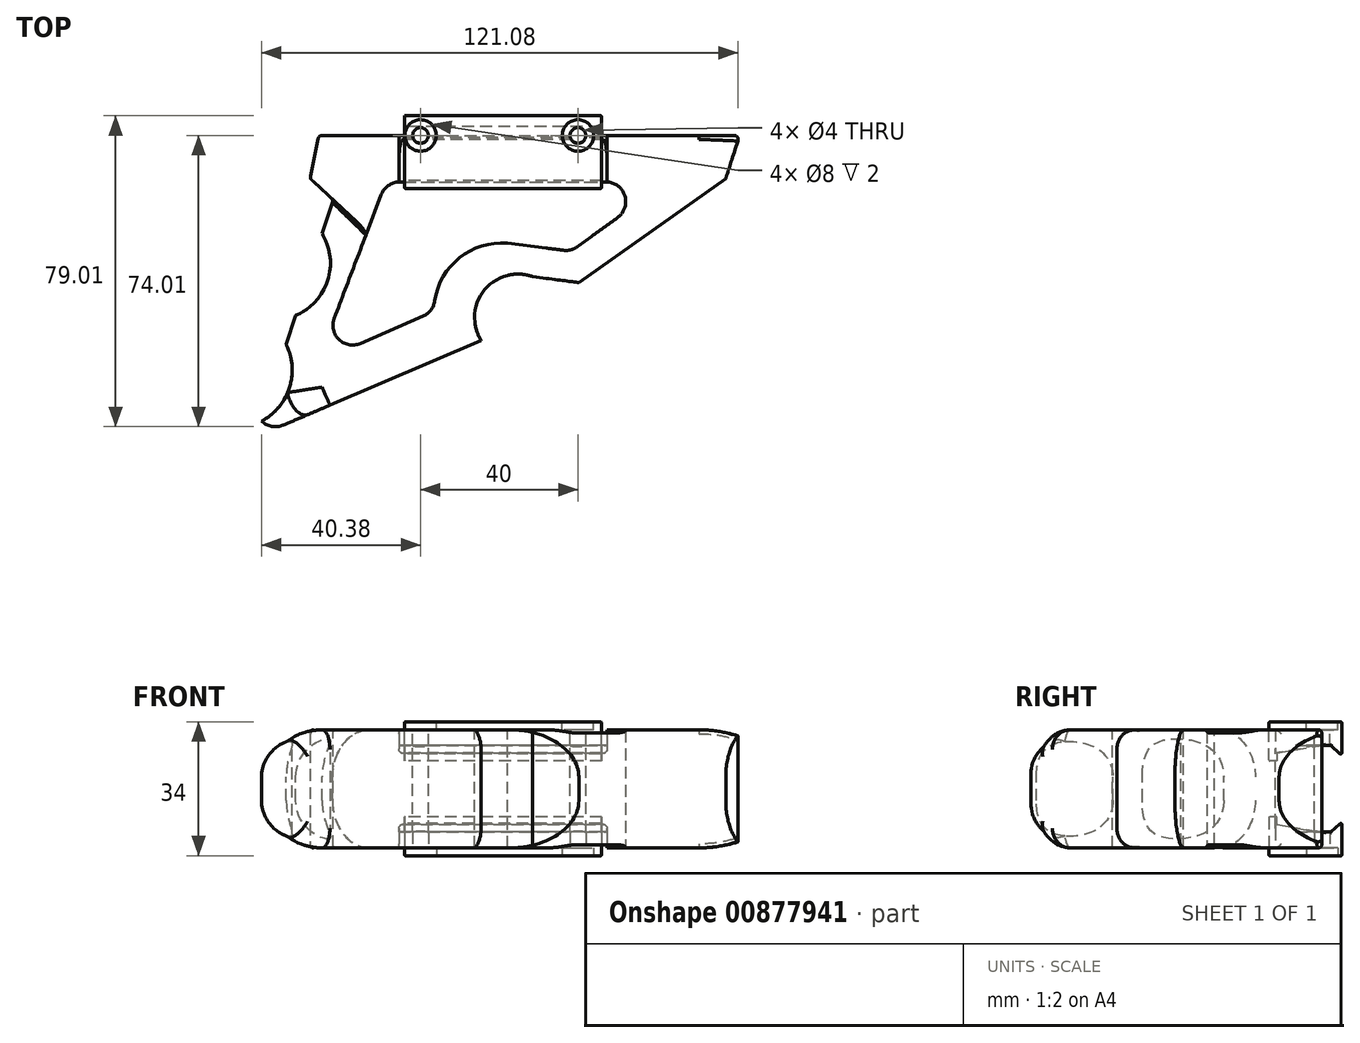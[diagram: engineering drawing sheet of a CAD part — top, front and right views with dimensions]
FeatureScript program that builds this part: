
annotation { "Feature Type Name" : "Feature", "Feature Type Description" : "" }
export const myFeature = defineFeature(function(context is Context, id is Id, definition is map)
    precondition{}
    {
        {
            var Q0;
            Q0=qCreatedBy(makeId("Top.planeOp"),FACE);
            var sketch = newSketch(context, id + "F0", { "sketchPlane" : qUnion([Q0])});
            skLineSegment(sketch, "E0", {"start": v(-36.24, 0) * mm, "end": v(-38.5, -10.92) * mm});
            skLineSegment(sketch, "E1", {"start": v(-38.5, -10.92) * mm, "end": v(-32.62, -16.35) * mm});
            skLineSegment(sketch, "E2", {"start": v(-32.62, -16.35) * mm, "end": v(-63.6, -112.26) * mm});
            skLineSegment(sketch, "E3", {"start": v(-63.6, -112.26) * mm, "end": v(-7.96, -123.8) * mm});
            skLineSegment(sketch, "E4", {"start": v(-7.96, -123.8) * mm, "end": v(16.02, -35.58) * mm});
            skLineSegment(sketch, "E5", {"start": v(16.02, -35.58) * mm, "end": v(29.82, -37.39) * mm});
            skLineSegment(sketch, "E6", {"start": v(29.82, -37.39) * mm, "end": v(67.14, -10.92) * mm});
            skLineSegment(sketch, "E7", {"start": v(67.14, -10.92) * mm, "end": v(70.67, 0) * mm});
            skLineSegment(sketch, "E8", {"start": v(-36.24, 0) * mm, "end": v(70.67, 0) * mm});
            skPoint(sketch, "E9.first.point", {"position": v(-35.48, -25.23) * mm});
            skPoint(sketch, "E9.second.point", {"position": v(-42.4, -46.63) * mm});
            skPoint(sketch, "E9.third.point", {"position": v(-65.03, -33.08) * mm});
            skPoint(sketch, "E10.first.point", {"position": v(-44.67, -53.65) * mm});
            skPoint(sketch, "E10.second.point", {"position": v(-50.9, -72.91) * mm});
            skPoint(sketch, "E10.third.point", {"position": v(-72.52, -56.97) * mm});
            skPoint(sketch, "E11.first.point", {"position": v(-54.13, -82.94) * mm});
            skPoint(sketch, "E11.second.point", {"position": v(-59.89, -100.75) * mm});
            skPoint(sketch, "E11.third.point", {"position": v(-85, -82.64) * mm});
            skLineSegment(sketch, "E12", {"start": v(-97.37, -25.23) * mm, "end": v(-7.02, -25.23) * mm, "construction": true});
            skLineSegment(sketch, "E13", {"start": v(-95.85, -46.63) * mm, "end": v(-7.4, -46.63) * mm, "construction": true});
            skLineSegment(sketch, "E14", {"start": v(-81.01, -53.65) * mm, "end": v(-12.15, -53.65) * mm, "construction": true});
            skLineSegment(sketch, "E15", {"start": v(-92.8, -72.91) * mm, "end": v(-15.2, -72.91) * mm, "construction": true});
            skLineSegment(sketch, "E16", {"start": v(-54.13, -82.94) * mm, "end": v(-73.21, -82.94) * mm});
            skLineSegment(sketch, "E17", {"start": v(-73.21, -82.94) * mm, "end": v(-28.9, -82.94) * mm, "construction": true});
            skLineSegment(sketch, "E18", {"start": v(-59.89, -100.75) * mm, "end": v(-91.1, -100.75) * mm});
            skLineSegment(sketch, "E19", {"start": v(-91.1, -100.75) * mm, "end": v(-23.57, -100.75) * mm, "construction": true});
            skLineSegment(sketch, "E20", {"start": v(-30.41, -25.23) * mm, "end": v(-60.21, -112.97) * mm, "construction": true});
            skSolve(sketch);
        }
        {
            var Q0;
            Q0=qSketchRegion(id+"F0",true);
            extrude(context, id + "F1", {"entities" : qUnion([Q0]), "endBound" : BoundingType.SYMMETRIC, "depth" : 30 * mm, "offsetDistance" : 25 * mm});
        }
        {
            var Q0;
            Q0=qCreatedBy(makeId("Top.planeOp"),FACE);
            var sketch = newSketch(context, id + "F2", { "sketchPlane" : qUnion([Q0])});
            skCircle(sketch, "E21", {"center": v(-47.66, -32.46) * mm, "radius": 14.36 * mm});
            skPoint(sketch, "E21.first.point", {"position": v(-35.59, -24.68) * mm});
            skPoint(sketch, "E21.second.point", {"position": v(-43.3, -46.15) * mm});
            skPoint(sketch, "E21.third.point", {"position": v(-61.39, -28.25) * mm});
            skCircle(sketch, "E22", {"center": v(-57.68, -59.62) * mm, "radius": 14.67 * mm});
            skPoint(sketch, "E22.first.point", {"position": v(-44.44, -53.3) * mm});
            skPoint(sketch, "E22.second.point", {"position": v(-51.03, -72.7) * mm});
            skPoint(sketch, "E22.third.point", {"position": v(-72.31, -58.58) * mm});
            skCircle(sketch, "E23", {"center": v(-69.65, -87.55) * mm, "radius": 16.16 * mm});
            skPoint(sketch, "E23.first.point", {"position": v(-54.23, -82.68) * mm});
            skPoint(sketch, "E23.second.point", {"position": v(-60.07, -100.57) * mm});
            skPoint(sketch, "E23.third.point", {"position": v(-85.5, -84.38) * mm});
            skCircle(sketch, "E24", {"center": v(-22.89, -107.96) * mm, "radius": 8.48 * mm});
            skPoint(sketch, "E24.first.point", {"position": v(-24.85, -116.2) * mm});
            skPoint(sketch, "E24.second.point", {"position": v(-20.52, -99.82) * mm});
            skPoint(sketch, "E24.third.point", {"position": v(-15.62, -103.59) * mm});
            skCircle(sketch, "E25", {"center": v(14.39, -46.27) * mm, "radius": 11.05 * mm});
            skPoint(sketch, "E25.first.point", {"position": v(16.03, -35.34) * mm});
            skPoint(sketch, "E25.second.point", {"position": v(10.2, -56.5) * mm});
            skPoint(sketch, "E25.third.point", {"position": v(23.76, -52.13) * mm});
            skCircle(sketch, "E26", {"center": v(14.16, -70.47) * mm, "radius": 11.31 * mm});
            skPoint(sketch, "E26.first.point", {"position": v(9.42, -60.2) * mm});
            skPoint(sketch, "E26.second.point", {"position": v(5.17, -77.33) * mm});
            skPoint(sketch, "E26.third.point", {"position": v(24.99, -73.75) * mm});
            skCircle(sketch, "E27", {"center": v(5.4, -101.86) * mm, "radius": 14.2 * mm});
            skPoint(sketch, "E27.first.point", {"position": v(2, -88.08) * mm});
            skPoint(sketch, "E27.second.point", {"position": v(-4.5, -112.05) * mm});
            skPoint(sketch, "E27.third.point", {"position": v(18.9, -106.22) * mm});
            skSolve(sketch);
        }
        {
            var Q0;
            Q0=qSketchRegion(id+"F2",true);
            extrude(context, id + "F3", {"entities" : qUnion([Q0]), "operationType" : NewBodyOperationType.REMOVE, "endBound" : BoundingType.SYMMETRIC, "oppositeDirection" : true, "depth" : 30 * mm, "offsetDistance" : 25 * mm});
        }
        {
            var Q0;
            {var subQ0=sQuery(id+"F2.wireOp",EDGE,"E22");Q0=makeQuery(id+"F3.boolean.opBoolean","COPY",EDGE,{"derivedFrom":makeQuery(id+"F3.opExtrude","CAP_EDGE",EDGE,{"disambiguationData":[OSD([subQ0]),TDD([makeQuery(id+"F2.imprint","IMPRINT",EDGE,{"disambiguationData":[TD([[makeQuery(id+"F2.imprint","INTERSECT",VERTEX,{"disambiguationData":[OD(1.0)],"derivedFrom":[sQuery(id+"F2.wireOp",EDGE,"E21"),subQ0]}),1.0]])],"derivedFrom":subQ0})])],"isStart":true})});}
            var Q1;
            Q1=makeQuery(id+"F3.boolean.opBoolean","COPY",EDGE,{"derivedFrom":makeQuery(id+"F3.opExtrude","CAP_EDGE",EDGE,{"disambiguationData":[OSD([sQuery(id+"F2.wireOp",EDGE,"E21")])],"isStart":true})});
            var Q2;
            Q2=makeQuery(id+"F3.boolean.opBoolean","COPY",EDGE,{"derivedFrom":makeQuery(id+"F3.opExtrude","CAP_EDGE",EDGE,{"disambiguationData":[OSD([sQuery(id+"F2.wireOp",EDGE,"E23")])],"isStart":true})});
            var Q3;
            Q3=makeQuery(id+"F3.boolean.opBoolean","COPY",EDGE,{"derivedFrom":makeQuery(id+"F3.opExtrude","CAP_EDGE",EDGE,{"disambiguationData":[OSD([sQuery(id+"F2.wireOp",EDGE,"E21")])],"isStart":false})});
            var Q4;
            {var subQ0=sQuery(id+"F2.wireOp",EDGE,"E22");Q4=makeQuery(id+"F3.boolean.opBoolean","COPY",EDGE,{"derivedFrom":makeQuery(id+"F3.opExtrude","CAP_EDGE",EDGE,{"disambiguationData":[OSD([subQ0]),TDD([makeQuery(id+"F2.imprint","IMPRINT",EDGE,{"disambiguationData":[TD([[makeQuery(id+"F2.imprint","INTERSECT",VERTEX,{"disambiguationData":[OD(1.0)],"derivedFrom":[sQuery(id+"F2.wireOp",EDGE,"E21"),subQ0]}),1.0]])],"derivedFrom":subQ0})])],"isStart":false})});}
            var Q5;
            Q5=makeQuery(id+"F3.boolean.opBoolean","COPY",EDGE,{"derivedFrom":makeQuery(id+"F3.opExtrude","CAP_EDGE",EDGE,{"disambiguationData":[OSD([sQuery(id+"F2.wireOp",EDGE,"E23")])],"isStart":false})});
            var Q6;
            {var subQ0=sQuery(id+"F0.wireOp",EDGE,"E2");var subQ1=sQuery(id+"F2.wireOp",EDGE,"E22");var subQ2=sQuery(id+"F2.wireOp",EDGE,"E23");Q6=makeQuery(id+"F3.boolean.opBoolean","SPLIT",EDGE,{"disambiguationData":[TD([makeQuery(id+"F1.opExtrude","CAP_FACE",FACE,{"disambiguationData":[OSD([sQuery(id+"F0.wireOp",EDGE,"E0"),sQuery(id+"F0.wireOp",EDGE,"E1"),subQ0,sQuery(id+"F0.wireOp",EDGE,"E3"),sQuery(id+"F0.wireOp",EDGE,"E4"),sQuery(id+"F0.wireOp",EDGE,"E5"),sQuery(id+"F0.wireOp",EDGE,"E6"),sQuery(id+"F0.wireOp",EDGE,"E7"),sQuery(id+"F0.wireOp",EDGE,"E8")])],"isStart":false}),makeQuery(id+"F1.opExtrude","SWEPT_FACE",FACE,{"disambiguationData":[OSD([subQ0])]}),makeQuery(id+"F3.opExtrude","SWEPT_FACE",FACE,{"disambiguationData":[OSD([subQ1]),TDD([makeQuery(id+"F2.imprint","IMPRINT",EDGE,{"disambiguationData":[TD([[makeQuery(id+"F2.imprint","INTERSECT",VERTEX,{"disambiguationData":[OD(1.0)],"derivedFrom":[sQuery(id+"F2.wireOp",EDGE,"E21"),subQ1]}),1.0]])],"derivedFrom":subQ1})])]}),makeQuery(id+"F3.opExtrude","SWEPT_FACE",FACE,{"disambiguationData":[OSD([subQ2])]})])],"derivedFrom":makeQuery(id+"F1.opExtrude","CAP_EDGE",EDGE,{"disambiguationData":[OSD([subQ0])],"isStart":false})});}
            var Q7;
            {var subQ0=sQuery(id+"F0.wireOp",EDGE,"E2");var subQ1=sQuery(id+"F2.wireOp",EDGE,"E22");var subQ2=sQuery(id+"F2.wireOp",EDGE,"E21");Q7=makeQuery(id+"F3.boolean.opBoolean","SPLIT",EDGE,{"disambiguationData":[TD([makeQuery(id+"F1.opExtrude","CAP_FACE",FACE,{"disambiguationData":[OSD([sQuery(id+"F0.wireOp",EDGE,"E0"),sQuery(id+"F0.wireOp",EDGE,"E1"),subQ0,sQuery(id+"F0.wireOp",EDGE,"E3"),sQuery(id+"F0.wireOp",EDGE,"E4"),sQuery(id+"F0.wireOp",EDGE,"E5"),sQuery(id+"F0.wireOp",EDGE,"E6"),sQuery(id+"F0.wireOp",EDGE,"E7"),sQuery(id+"F0.wireOp",EDGE,"E8")])],"isStart":false}),makeQuery(id+"F1.opExtrude","SWEPT_FACE",FACE,{"disambiguationData":[OSD([subQ0])]}),makeQuery(id+"F3.opExtrude","SWEPT_FACE",FACE,{"disambiguationData":[OSD([subQ2])]}),makeQuery(id+"F3.opExtrude","SWEPT_FACE",FACE,{"disambiguationData":[OSD([subQ1]),TDD([makeQuery(id+"F2.imprint","IMPRINT",EDGE,{"disambiguationData":[TD([[makeQuery(id+"F2.imprint","INTERSECT",VERTEX,{"disambiguationData":[OD(1.0)],"derivedFrom":[subQ2,subQ1]}),1.0]])],"derivedFrom":subQ1})])]})])],"derivedFrom":makeQuery(id+"F1.opExtrude","CAP_EDGE",EDGE,{"disambiguationData":[OSD([subQ0])],"isStart":false})});}
            var Q8;
            {var subQ0=sQuery(id+"F0.wireOp",EDGE,"E2");var subQ1=sQuery(id+"F2.wireOp",EDGE,"E22");var subQ2=sQuery(id+"F2.wireOp",EDGE,"E23");Q8=makeQuery(id+"F3.boolean.opBoolean","SPLIT",EDGE,{"disambiguationData":[TD([makeQuery(id+"F1.opExtrude","CAP_FACE",FACE,{"disambiguationData":[OSD([sQuery(id+"F0.wireOp",EDGE,"E0"),sQuery(id+"F0.wireOp",EDGE,"E1"),subQ0,sQuery(id+"F0.wireOp",EDGE,"E3"),sQuery(id+"F0.wireOp",EDGE,"E4"),sQuery(id+"F0.wireOp",EDGE,"E5"),sQuery(id+"F0.wireOp",EDGE,"E6"),sQuery(id+"F0.wireOp",EDGE,"E7"),sQuery(id+"F0.wireOp",EDGE,"E8")])],"isStart":true}),makeQuery(id+"F1.opExtrude","SWEPT_FACE",FACE,{"disambiguationData":[OSD([subQ0])]}),makeQuery(id+"F3.opExtrude","SWEPT_FACE",FACE,{"disambiguationData":[OSD([subQ1]),TDD([makeQuery(id+"F2.imprint","IMPRINT",EDGE,{"disambiguationData":[TD([[makeQuery(id+"F2.imprint","INTERSECT",VERTEX,{"disambiguationData":[OD(1.0)],"derivedFrom":[sQuery(id+"F2.wireOp",EDGE,"E21"),subQ1]}),1.0]])],"derivedFrom":subQ1})])]}),makeQuery(id+"F3.opExtrude","SWEPT_FACE",FACE,{"disambiguationData":[OSD([subQ2])]})])],"derivedFrom":makeQuery(id+"F1.opExtrude","CAP_EDGE",EDGE,{"disambiguationData":[OSD([subQ0])],"isStart":true})});}
            var Q9;
            {var subQ0=sQuery(id+"F0.wireOp",EDGE,"E2");var subQ1=sQuery(id+"F2.wireOp",EDGE,"E21");var subQ2=sQuery(id+"F2.wireOp",EDGE,"E22");Q9=makeQuery(id+"F3.boolean.opBoolean","SPLIT",EDGE,{"disambiguationData":[TD([makeQuery(id+"F1.opExtrude","CAP_FACE",FACE,{"disambiguationData":[OSD([sQuery(id+"F0.wireOp",EDGE,"E0"),sQuery(id+"F0.wireOp",EDGE,"E1"),subQ0,sQuery(id+"F0.wireOp",EDGE,"E3"),sQuery(id+"F0.wireOp",EDGE,"E4"),sQuery(id+"F0.wireOp",EDGE,"E5"),sQuery(id+"F0.wireOp",EDGE,"E6"),sQuery(id+"F0.wireOp",EDGE,"E7"),sQuery(id+"F0.wireOp",EDGE,"E8")])],"isStart":true}),makeQuery(id+"F1.opExtrude","SWEPT_FACE",FACE,{"disambiguationData":[OSD([subQ0])]}),makeQuery(id+"F3.opExtrude","SWEPT_FACE",FACE,{"disambiguationData":[OSD([subQ1])]}),makeQuery(id+"F3.opExtrude","SWEPT_FACE",FACE,{"disambiguationData":[OSD([subQ2]),TDD([makeQuery(id+"F2.imprint","IMPRINT",EDGE,{"disambiguationData":[TD([[makeQuery(id+"F2.imprint","INTERSECT",VERTEX,{"disambiguationData":[OD(1.0)],"derivedFrom":[subQ1,subQ2]}),1.0]])],"derivedFrom":subQ2})])]})])],"derivedFrom":makeQuery(id+"F1.opExtrude","CAP_EDGE",EDGE,{"disambiguationData":[OSD([subQ0])],"isStart":true})});}
            var Q10;
            Q10=makeQuery(id+"F3.boolean.opBoolean","COPY",EDGE,{"derivedFrom":makeQuery(id+"F3.opExtrude","CAP_EDGE",EDGE,{"disambiguationData":[OSD([sQuery(id+"F2.wireOp",EDGE,"E25")])],"isStart":true})});
            var Q11;
            Q11=makeQuery(id+"F3.boolean.opBoolean","COPY",EDGE,{"derivedFrom":makeQuery(id+"F3.opExtrude","CAP_EDGE",EDGE,{"disambiguationData":[OSD([sQuery(id+"F2.wireOp",EDGE,"E26")])],"isStart":true})});
            var Q12;
            Q12=makeQuery(id+"F3.boolean.opBoolean","COPY",EDGE,{"derivedFrom":makeQuery(id+"F3.opExtrude","CAP_EDGE",EDGE,{"disambiguationData":[OSD([sQuery(id+"F2.wireOp",EDGE,"E27")])],"isStart":true})});
            var Q13;
            Q13=makeQuery(id+"F3.boolean.opBoolean","COPY",EDGE,{"derivedFrom":makeQuery(id+"F3.opExtrude","CAP_EDGE",EDGE,{"disambiguationData":[OSD([sQuery(id+"F2.wireOp",EDGE,"E27")])],"isStart":false})});
            var Q14;
            Q14=makeQuery(id+"F3.boolean.opBoolean","COPY",EDGE,{"derivedFrom":makeQuery(id+"F3.opExtrude","CAP_EDGE",EDGE,{"disambiguationData":[OSD([sQuery(id+"F2.wireOp",EDGE,"E26")])],"isStart":false})});
            var Q15;
            Q15=makeQuery(id+"F3.boolean.opBoolean","COPY",EDGE,{"derivedFrom":makeQuery(id+"F3.opExtrude","CAP_EDGE",EDGE,{"disambiguationData":[OSD([sQuery(id+"F2.wireOp",EDGE,"E25")])],"isStart":false})});
            var Q16;
            Q16=makeQuery(id+"F1.opExtrude","CAP_EDGE",EDGE,{"disambiguationData":[OSD([sQuery(id+"F0.wireOp",EDGE,"E6")])],"isStart":true});
            var Q17;
            Q17=makeQuery(id+"F1.opExtrude","CAP_EDGE",EDGE,{"disambiguationData":[OSD([sQuery(id+"F0.wireOp",EDGE,"E6")])],"isStart":false});
            var Q18;
            Q18=makeQuery(id+"F1.opExtrude","CAP_EDGE",EDGE,{"disambiguationData":[OSD([sQuery(id+"F0.wireOp",EDGE,"E3")])],"isStart":true});
            var Q19;
            Q19=makeQuery(id+"F1.opExtrude","CAP_EDGE",EDGE,{"disambiguationData":[OSD([sQuery(id+"F0.wireOp",EDGE,"E3")])],"isStart":false});
            fillet(context, id + "F4", {"entities" : qUnion([Q0, Q1, Q2, Q3, Q4, Q5, Q6, Q7, Q8, Q9, Q10, Q11, Q12, Q13, Q14, Q15, Q16, Q17, Q18, Q19]), "radius" : 12 * mm, "tangentPropagation" : true, "allowEdgeOverflow" : false});
        }
        {
            var Q0;
            Q0=makeQuery(id+"F1.opExtrude","SWEPT_EDGE",EDGE,{"disambiguationData":[OSD([sQuery(id+"F0.wireOp",EDGE,"E1"),sQuery(id+"F0.wireOp",EDGE,"E2")])]});
            var Q1;
            Q1=makeQuery(id+"F1.opExtrude","SWEPT_EDGE",EDGE,{"disambiguationData":[OSD([sQuery(id+"F0.wireOp",EDGE,"E0"),sQuery(id+"F0.wireOp",EDGE,"E1")])]});
            var Q2;
            Q2=makeQuery(id+"F1.opExtrude","SWEPT_EDGE",EDGE,{"disambiguationData":[OSD([sQuery(id+"F0.wireOp",EDGE,"E0"),sQuery(id+"F0.wireOp",EDGE,"E8")])]});
            var Q3;
            Q3=makeQuery(id+"F1.opExtrude","SWEPT_EDGE",EDGE,{"disambiguationData":[OSD([sQuery(id+"F0.wireOp",EDGE,"E7"),sQuery(id+"F0.wireOp",EDGE,"E8")])]});
            var Q4;
            Q4=makeQuery(id+"F1.opExtrude","CAP_EDGE",EDGE,{"disambiguationData":[OSD([sQuery(id+"F0.wireOp",EDGE,"E8")])],"isStart":false});
            var Q5;
            Q5=makeQuery(id+"F1.opExtrude","CAP_EDGE",EDGE,{"disambiguationData":[OSD([sQuery(id+"F0.wireOp",EDGE,"E8")])],"isStart":true});
            var Q6;
            Q6=makeQuery(id+"F1.opExtrude","CAP_EDGE",EDGE,{"disambiguationData":[OSD([sQuery(id+"F0.wireOp",EDGE,"E0")])],"isStart":false});
            var Q7;
            Q7=makeQuery(id+"F1.opExtrude","CAP_EDGE",EDGE,{"disambiguationData":[OSD([sQuery(id+"F0.wireOp",EDGE,"E0")])],"isStart":true});
            fillet(context, id + "F5", {"entities" : qUnion([Q0, Q1, Q2, Q3, Q4, Q5, Q6, Q7]), "radius" : 1 * mm, "tangentPropagation" : true, "allowEdgeOverflow" : false});
        }
        {
            var Q0;
            Q0=qCreatedBy(makeId("Top.planeOp"),FACE);
            var sketch = newSketch(context, id + "F6", { "sketchPlane" : qUnion([Q0])});
            skLineSegment(sketch, "E28", {"start": v(-50.63, -99.24) * mm, "end": v(-41.6, -72.02) * mm});
            skLineSegment(sketch, "E29", {"start": v(-41.6, -72.02) * mm, "end": v(-2.6, -55.36) * mm});
            skLineSegment(sketch, "E30", {"start": v(-2.6, -55.36) * mm, "end": v(-12.68, -83.42) * mm});
            skLineSegment(sketch, "E31", {"start": v(-12.68, -83.42) * mm, "end": v(-50.63, -99.24) * mm});
            skLineSegment(sketch, "E32", {"start": v(-36.57, -57.58) * mm, "end": v(-19.15, -11.81) * mm});
            skLineSegment(sketch, "E33", {"start": v(-19.15, -11.81) * mm, "end": v(52.14, -11.81) * mm});
            skLineSegment(sketch, "E34", {"start": v(52.14, -11.81) * mm, "end": v(27.84, -29.42) * mm});
            skLineSegment(sketch, "E35", {"start": v(27.84, -29.42) * mm, "end": v(11.65, -27.35) * mm});
            skLineSegment(sketch, "E36", {"start": v(-36.57, -57.58) * mm, "end": v(-7, -44.68) * mm});
            skArc(sketch, "E37", {"start": v(13.34, -27.57) * mm, "mid": v(-0.83, -31.36) * mm, "end": v(-7, -44.68) * mm});
            skPoint(sketch, "E37.third.point", {"position": v(24.64, -54.28) * mm});
            skSolve(sketch);
        }
        {
            var Q0;
            Q0=qSketchRegion(id+"F6",true);
            extrude(context, id + "F7", {"entities" : qUnion([Q0]), "operationType" : NewBodyOperationType.REMOVE, "endBound" : BoundingType.SYMMETRIC, "oppositeDirection" : true, "depth" : 30 * mm, "offsetDistance" : 25 * mm});
        }
        {
            var Q0;
            Q0=makeQuery(id+"F4.opFillet","BLEND_EDGE",EDGE,{"blendedFrom":[makeQuery(id+"F1.opExtrude","CAP_EDGE",EDGE,{"disambiguationData":[OSD([sQuery(id+"F0.wireOp",EDGE,"E3")])],"isStart":false}),makeQuery(id+"F3.boolean.opBoolean","COPY",FACE,{"derivedFrom":makeQuery(id+"F3.opExtrude","SWEPT_FACE",FACE,{"disambiguationData":[OSD([sQuery(id+"F2.wireOp",EDGE,"E24")])]})})],"blendedInto":[makeQuery(id+"F3.boolean.opBoolean","COPY",FACE,{"derivedFrom":makeQuery(id+"F3.opExtrude","SWEPT_FACE",FACE,{"disambiguationData":[OSD([sQuery(id+"F2.wireOp",EDGE,"E24")])]})})]});
            var Q1;
            Q1=makeQuery(id+"F4.opFillet","BLEND_EDGE",EDGE,{"blendedFrom":[makeQuery(id+"F1.opExtrude","CAP_EDGE",EDGE,{"disambiguationData":[OSD([sQuery(id+"F0.wireOp",EDGE,"E3")])],"isStart":true}),makeQuery(id+"F3.boolean.opBoolean","COPY",FACE,{"derivedFrom":makeQuery(id+"F3.opExtrude","SWEPT_FACE",FACE,{"disambiguationData":[OSD([sQuery(id+"F2.wireOp",EDGE,"E24")])]})})],"blendedInto":[makeQuery(id+"F3.boolean.opBoolean","COPY",FACE,{"derivedFrom":makeQuery(id+"F3.opExtrude","SWEPT_FACE",FACE,{"disambiguationData":[OSD([sQuery(id+"F2.wireOp",EDGE,"E24")])]})})]});
            fillet(context, id + "F8", {"entities" : qUnion([Q0, Q1]), "radius" : 1 * mm, "tangentPropagation" : true, "allowEdgeOverflow" : false});
        }
        {
            var Q0;
            Q0=makeQuery(id+"F7.boolean.opBoolean","COPY",EDGE,{"derivedFrom":makeQuery(id+"F7.opExtrude","SWEPT_EDGE",EDGE,{"disambiguationData":[OSD([sQuery(id+"F6.wireOp",EDGE,"E28"),sQuery(id+"F6.wireOp",EDGE,"E31")])]})});
            var Q1;
            Q1=makeQuery(id+"F7.boolean.opBoolean","COPY",EDGE,{"derivedFrom":makeQuery(id+"F7.opExtrude","SWEPT_EDGE",EDGE,{"disambiguationData":[OSD([sQuery(id+"F6.wireOp",EDGE,"E29"),sQuery(id+"F6.wireOp",EDGE,"E30")])]})});
            var Q2;
            Q2=makeQuery(id+"F7.boolean.opBoolean","COPY",EDGE,{"derivedFrom":makeQuery(id+"F7.opExtrude","SWEPT_EDGE",EDGE,{"disambiguationData":[OSD([sQuery(id+"F6.wireOp",EDGE,"E28"),sQuery(id+"F6.wireOp",EDGE,"E29")])]})});
            var Q3;
            Q3=makeQuery(id+"F7.boolean.opBoolean","COPY",EDGE,{"derivedFrom":makeQuery(id+"F7.opExtrude","SWEPT_EDGE",EDGE,{"disambiguationData":[OSD([sQuery(id+"F6.wireOp",EDGE,"E30"),sQuery(id+"F6.wireOp",EDGE,"E31")])]})});
            var Q4;
            Q4=makeQuery(id+"F7.boolean.opBoolean","COPY",EDGE,{"derivedFrom":makeQuery(id+"F7.opExtrude","SWEPT_EDGE",EDGE,{"disambiguationData":[OSD([sQuery(id+"F6.wireOp",EDGE,"E32"),sQuery(id+"F6.wireOp",EDGE,"E36")])]})});
            var Q5;
            Q5=makeQuery(id+"F7.boolean.opBoolean","COPY",EDGE,{"derivedFrom":makeQuery(id+"F7.opExtrude","SWEPT_EDGE",EDGE,{"disambiguationData":[OSD([sQuery(id+"F6.wireOp",EDGE,"E32"),sQuery(id+"F6.wireOp",EDGE,"E33")])]})});
            var Q6;
            Q6=makeQuery(id+"F7.boolean.opBoolean","COPY",EDGE,{"derivedFrom":makeQuery(id+"F7.opExtrude","SWEPT_EDGE",EDGE,{"disambiguationData":[OSD([sQuery(id+"F6.wireOp",EDGE,"E33"),sQuery(id+"F6.wireOp",EDGE,"E34")])]})});
            var Q7;
            Q7=makeQuery(id+"F7.boolean.opBoolean","COPY",EDGE,{"derivedFrom":makeQuery(id+"F7.opExtrude","SWEPT_EDGE",EDGE,{"disambiguationData":[OSD([sQuery(id+"F6.wireOp",EDGE,"E34"),sQuery(id+"F6.wireOp",EDGE,"E35")])]})});
            var Q8;
            Q8=makeQuery(id+"F7.boolean.opBoolean","COPY",EDGE,{"derivedFrom":makeQuery(id+"F7.opExtrude","SWEPT_EDGE",EDGE,{"disambiguationData":[OSD([sQuery(id+"F6.wireOp",EDGE,"E36"),sQuery(id+"F6.wireOp",EDGE,"E37")])]})});
            fillet(context, id + "F9", {"entities" : qUnion([Q0, Q1, Q2, Q3, Q4, Q5, Q6, Q7, Q8]), "radius" : 5 * mm, "tangentPropagation" : true, "allowEdgeOverflow" : false});
        }
        {
            var Q0;
            Q0=qCreatedBy(makeId("Right.planeOp"),FACE);
            var sketch = newSketch(context, id + "F10", { "sketchPlane" : qUnion([Q0])});
            skLineSegment(sketch, "E38", {"start": v(-1, 11) * mm, "end": v(-11.96, 9.07) * mm});
            skLineSegment(sketch, "E39", {"start": v(-11.96, 13.97) * mm, "end": v(-11.96, 9.07) * mm});
            skLineSegment(sketch, "E40", {"start": v(0, 0) * mm, "end": v(-125.67, 0) * mm, "construction": true});
            skLineSegment(sketch, "E41.MirrorCS", {"start": v(-1, -11) * mm, "end": v(-11.96, -9.07) * mm});
            skLineSegment(sketch, "E42.MirrorCS", {"start": v(-1, -17.8) * mm, "end": v(-11.96, -17.8) * mm});
            skLineSegment(sketch, "E43.MirrorCS", {"start": v(-11.96, -17.8) * mm, "end": v(-11.96, -9.07) * mm});
            skLineSegment(sketch, "E44.top", {"start": v(-1, 11) * mm, "end": v(1.5, 11) * mm});
            skLineSegment(sketch, "E44.right", {"start": v(1.5, 13.97) * mm, "end": v(1.5, 11) * mm});
            skLineSegment(sketch, "E45.bottom", {"start": v(-1, -11) * mm, "end": v(1.5, -11) * mm});
            skLineSegment(sketch, "E45.top", {"start": v(-1, -17.8) * mm, "end": v(1.5, -17.8) * mm});
            skLineSegment(sketch, "E45.right", {"start": v(1.5, -11) * mm, "end": v(1.5, -17.8) * mm});
            skLineSegment(sketch, "E46.top", {"start": v(-11.96, 17.3) * mm, "end": v(1.5, 17.3) * mm});
            skLineSegment(sketch, "E46.left", {"start": v(-11.96, 13.97) * mm, "end": v(-11.96, 17.3) * mm});
            skLineSegment(sketch, "E46.right", {"start": v(1.5, 13.97) * mm, "end": v(1.5, 17.3) * mm});
            skSolve(sketch);
        }
        {
            var Q0;
            Q0=qSketchRegion(id+"F10",true);
            extrude(context, id + "F11", {"entities" : qUnion([Q0]), "operationType" : NewBodyOperationType.REMOVE, "depth" : 37 * mm, "offsetDistance" : 25 * mm, "hasSecondDirection" : true, "secondDirectionOppositeDirection" : true, "secondDirectionDepth" : 15.9 * mm});
        }
        {
            var Q0;
            Q0=makeQuery(id+"F11.boolean.opBoolean","COPY",EDGE,{"derivedFrom":makeQuery(id+"F11.opExtrude","CAP_EDGE",EDGE,{"disambiguationData":[OSD([sQuery(id+"F10.wireOp",EDGE,"E38")])],"isStart":true})});
            var Q1;
            Q1=makeQuery(id+"F11.boolean.opBoolean","COPY",EDGE,{"derivedFrom":makeQuery(id+"F11.opExtrude","CAP_EDGE",EDGE,{"disambiguationData":[OSD([sQuery(id+"F10.wireOp",EDGE,"E38")])],"isStart":false})});
            var Q2;
            Q2=makeQuery(id+"F11.boolean.opBoolean","COPY",EDGE,{"derivedFrom":makeQuery(id+"F11.opExtrude","CAP_EDGE",EDGE,{"disambiguationData":[OSD([sQuery(id+"F10.wireOp",EDGE,"E41.MirrorCS")])],"isStart":false})});
            var Q3;
            Q3=makeQuery(id+"F11.boolean.opBoolean","COPY",EDGE,{"derivedFrom":makeQuery(id+"F11.opExtrude","CAP_EDGE",EDGE,{"disambiguationData":[OSD([sQuery(id+"F10.wireOp",EDGE,"E41.MirrorCS")])],"isStart":true})});
            fillet(context, id + "F12", {"entities" : qUnion([Q0, Q1, Q2, Q3]), "radius" : 1 * mm, "tangentPropagation" : true, "allowEdgeOverflow" : false});
        }
        {
            var Q0;
            Q0=qCreatedBy(makeId("Right.planeOp"),FACE);
            var sketch = newSketch(context, id + "F13", { "sketchPlane" : qUnion([Q0])});
            skPoint(sketch, "E47", {"position": v(-11.48, 9.07) * mm});
            skPoint(sketch, "E48", {"position": v(-0.51, 11) * mm});
            skPoint(sketch, "E49", {"position": v(1.99, 11) * mm});
            skLineSegment(sketch, "E50", {"start": v(-11.48, 9.07) * mm, "end": v(-0.51, 11) * mm});
            skLineSegment(sketch, "E51", {"start": v(-11.48, 9.07) * mm, "end": v(-11.48, 7.07) * mm});
            skLineSegment(sketch, "E52", {"start": v(-11.48, 7.07) * mm, "end": v(-13.48, 7.07) * mm});
            skLineSegment(sketch, "E53", {"start": v(-13.48, 7.07) * mm, "end": v(-13.48, 17) * mm});
            skLineSegment(sketch, "E54", {"start": v(5, 11) * mm, "end": v(5, 17) * mm});
            skLineSegment(sketch, "E55", {"start": v(5, 17) * mm, "end": v(-13.48, 17) * mm});
            skLineSegment(sketch, "E56", {"start": v(5, 8.5) * mm, "end": v(5, 11) * mm});
            skLineSegment(sketch, "E57", {"start": v(2.24, 11) * mm, "end": v(5, 8.5) * mm});
            skLineSegment(sketch, "E58", {"start": v(-0.51, 11) * mm, "end": v(2.24, 11) * mm});
            skLineSegment(sketch, "E59.MirrorCS", {"start": v(-11.48, -7.07) * mm, "end": v(-13.48, -7.07) * mm});
            skLineSegment(sketch, "E60.MirrorCS", {"start": v(-11.48, -9.07) * mm, "end": v(-11.48, -7.07) * mm});
            skLineSegment(sketch, "E61.MirrorCS", {"start": v(-0.51, -11) * mm, "end": v(2.24, -11) * mm});
            skPoint(sketch, "E62.MirrorP", {"position": v(-11.48, -9.07) * mm});
            skLineSegment(sketch, "E63.MirrorCS", {"start": v(-11.48, -9.07) * mm, "end": v(-0.51, -11) * mm});
            skLineSegment(sketch, "E64.MirrorCS", {"start": v(5, -17) * mm, "end": v(-13.48, -17) * mm});
            skLineSegment(sketch, "E65.MirrorCS", {"start": v(5, -11) * mm, "end": v(5, -17) * mm});
            skPoint(sketch, "E66.MirrorP", {"position": v(1.99, -11) * mm});
            skLineSegment(sketch, "E67.MirrorCS", {"start": v(5, -8.5) * mm, "end": v(5, -11) * mm});
            skLineSegment(sketch, "E68.MirrorCS", {"start": v(2.24, -11) * mm, "end": v(5, -8.5) * mm});
            skLineSegment(sketch, "E69.MirrorCS", {"start": v(-13.48, -7.07) * mm, "end": v(-13.48, -17) * mm});
            skPoint(sketch, "E70.MirrorP", {"position": v(-0.51, -11) * mm});
            skSolve(sketch);
        }
        {
            var Q0;
            Q0=qSketchRegion(id+"F13",true);
            extrude(context, id + "F14", {"entities" : qUnion([Q0]), "depth" : 35.6 * mm, "offsetDistance" : 25 * mm, "hasSecondDirection" : true, "secondDirectionOppositeDirection" : true, "secondDirectionDepth" : 14.5 * mm});
        }
        {
            var Q0;
            Q0=makeQuery(id+"F14.opExtrude","SWEPT_FACE",FACE,{"disambiguationData":[OSD([sQuery(id+"F13.wireOp",EDGE,"E55")])]});
            var sketch = newSketch(context, id + "F15", { "sketchPlane" : qUnion([Q0])});
            skPoint(sketch, "E71", {"position": v(29.6, 0) * mm});
            skPoint(sketch, "E72", {"position": v(-10.4, 0) * mm});
            skSolve(sketch);
        }
        {
            var Q0;
            Q0=sQuery(id+"F15.wireOp",VERTEX,"E71");
            var Q1;
            Q1=sQuery(id+"F15.wireOp",VERTEX,"E72");
            var Q2;
            Q2=makeQuery(id+"F14.opExtrude","SWEPT_BODY",BODY,{"disambiguationData":[OSD([sQuery(id+"F13.wireOp",EDGE,"E50"),sQuery(id+"F13.wireOp",EDGE,"E51"),sQuery(id+"F13.wireOp",EDGE,"E52"),sQuery(id+"F13.wireOp",EDGE,"E53"),sQuery(id+"F13.wireOp",EDGE,"E54"),sQuery(id+"F13.wireOp",EDGE,"E55"),sQuery(id+"F13.wireOp",EDGE,"E56"),sQuery(id+"F13.wireOp",EDGE,"E57"),sQuery(id+"F13.wireOp",EDGE,"E58")])]});
            var Q3;
            Q3=makeQuery(id+"F1.opExtrude","SWEPT_BODY",BODY,{"disambiguationData":[OSD([sQuery(id+"F0.wireOp",EDGE,"E0"),sQuery(id+"F0.wireOp",EDGE,"E1"),sQuery(id+"F0.wireOp",EDGE,"E2"),sQuery(id+"F0.wireOp",EDGE,"E3"),sQuery(id+"F0.wireOp",EDGE,"E4"),sQuery(id+"F0.wireOp",EDGE,"E5"),sQuery(id+"F0.wireOp",EDGE,"E6"),sQuery(id+"F0.wireOp",EDGE,"E7"),sQuery(id+"F0.wireOp",EDGE,"E8")])]});
            hole(context, id + "F16", {"style" : HoleStyle.C_BORE, "endStyle" : HoleEndStyle.BLIND, "holeDiameter" : 4 * mm, "cBoreDiameter" : 8 * mm, "cBoreDepth" : 2 * mm, "majorDiameter" : 5 * mm, "holeDepth" : 40 * mm, "isTappedThrough" : true, "tappedDepth" : 12 * mm, "tapClearance" : 3, "startFromSketch" : true, "locations" : qUnion([Q0, Q1]), "scope" : qUnion([Q2, Q3])});
        }
        {
            var Q0;
            Q0=makeQuery(id+"F14.opExtrude","SWEPT_EDGE",EDGE,{"disambiguationData":[OSD([sQuery(id+"F13.wireOp",EDGE,"E56"),sQuery(id+"F13.wireOp",EDGE,"E57")])]});
            var Q1;
            Q1=makeQuery(id+"F14.opExtrude","SWEPT_EDGE",EDGE,{"disambiguationData":[OSD([sQuery(id+"F13.wireOp",EDGE,"E67.MirrorCS"),sQuery(id+"F13.wireOp",EDGE,"E68.MirrorCS")])]});
            var Q2;
            Q2=makeQuery(id+"F14.opExtrude","SWEPT_EDGE",EDGE,{"disambiguationData":[OSD([sQuery(id+"F13.wireOp",EDGE,"E54"),sQuery(id+"F13.wireOp",EDGE,"E55")])]});
            var Q3;
            Q3=makeQuery(id+"F14.opExtrude","SWEPT_EDGE",EDGE,{"disambiguationData":[OSD([sQuery(id+"F13.wireOp",EDGE,"E64.MirrorCS"),sQuery(id+"F13.wireOp",EDGE,"E65.MirrorCS")])]});
            var Q4;
            Q4=makeQuery(id+"F14.opExtrude","CAP_EDGE",EDGE,{"disambiguationData":[OSD([sQuery(id+"F13.wireOp",EDGE,"E65.MirrorCS"),sQuery(id+"F13.wireOp",EDGE,"E67.MirrorCS")])],"isStart":false});
            var Q5;
            Q5=makeQuery(id+"F14.opExtrude","CAP_EDGE",EDGE,{"disambiguationData":[OSD([sQuery(id+"F13.wireOp",EDGE,"E65.MirrorCS"),sQuery(id+"F13.wireOp",EDGE,"E67.MirrorCS")])],"isStart":true});
            var Q6;
            Q6=makeQuery(id+"F14.opExtrude","CAP_EDGE",EDGE,{"disambiguationData":[OSD([sQuery(id+"F13.wireOp",EDGE,"E68.MirrorCS")])],"isStart":false});
            var Q7;
            Q7=makeQuery(id+"F14.opExtrude","CAP_EDGE",EDGE,{"disambiguationData":[OSD([sQuery(id+"F13.wireOp",EDGE,"E61.MirrorCS")])],"isStart":false});
            var Q8;
            Q8=makeQuery(id+"F14.opExtrude","CAP_EDGE",EDGE,{"disambiguationData":[OSD([sQuery(id+"F13.wireOp",EDGE,"E64.MirrorCS")])],"isStart":false});
            var Q9;
            Q9=makeQuery(id+"F14.opExtrude","CAP_EDGE",EDGE,{"disambiguationData":[OSD([sQuery(id+"F13.wireOp",EDGE,"E54"),sQuery(id+"F13.wireOp",EDGE,"E56")])],"isStart":false});
            var Q10;
            Q10=makeQuery(id+"F14.opExtrude","CAP_EDGE",EDGE,{"disambiguationData":[OSD([sQuery(id+"F13.wireOp",EDGE,"E57")])],"isStart":false});
            var Q11;
            Q11=makeQuery(id+"F14.opExtrude","CAP_EDGE",EDGE,{"disambiguationData":[OSD([sQuery(id+"F13.wireOp",EDGE,"E58")])],"isStart":false});
            var Q12;
            Q12=makeQuery(id+"F14.opExtrude","CAP_EDGE",EDGE,{"disambiguationData":[OSD([sQuery(id+"F13.wireOp",EDGE,"E55")])],"isStart":false});
            var Q13;
            Q13=makeQuery(id+"F14.opExtrude","CAP_EDGE",EDGE,{"disambiguationData":[OSD([sQuery(id+"F13.wireOp",EDGE,"E53")])],"isStart":false});
            var Q14;
            Q14=makeQuery(id+"F14.opExtrude","CAP_EDGE",EDGE,{"disambiguationData":[OSD([sQuery(id+"F13.wireOp",EDGE,"E55")])],"isStart":true});
            var Q15;
            Q15=makeQuery(id+"F14.opExtrude","CAP_EDGE",EDGE,{"disambiguationData":[OSD([sQuery(id+"F13.wireOp",EDGE,"E57")])],"isStart":true});
            var Q16;
            Q16=makeQuery(id+"F14.opExtrude","CAP_EDGE",EDGE,{"disambiguationData":[OSD([sQuery(id+"F13.wireOp",EDGE,"E58")])],"isStart":true});
            var Q17;
            Q17=makeQuery(id+"F14.opExtrude","SWEPT_EDGE",EDGE,{"disambiguationData":[OSD([sQuery(id+"F13.wireOp",EDGE,"E53"),sQuery(id+"F13.wireOp",EDGE,"E55")])]});
            var Q18;
            Q18=makeQuery(id+"F14.opExtrude","CAP_EDGE",EDGE,{"disambiguationData":[OSD([sQuery(id+"F13.wireOp",EDGE,"E53")])],"isStart":true});
            var Q19;
            Q19=makeQuery(id+"F14.opExtrude","SWEPT_EDGE",EDGE,{"disambiguationData":[OSD([sQuery(id+"F13.wireOp",EDGE,"E52"),sQuery(id+"F13.wireOp",EDGE,"E53")])]});
            var Q20;
            Q20=makeQuery(id+"F14.opExtrude","CAP_EDGE",EDGE,{"disambiguationData":[OSD([sQuery(id+"F13.wireOp",EDGE,"E64.MirrorCS")])],"isStart":true});
            var Q21;
            Q21=makeQuery(id+"F14.opExtrude","CAP_EDGE",EDGE,{"disambiguationData":[OSD([sQuery(id+"F13.wireOp",EDGE,"E68.MirrorCS")])],"isStart":true});
            var Q22;
            Q22=makeQuery(id+"F14.opExtrude","CAP_EDGE",EDGE,{"disambiguationData":[OSD([sQuery(id+"F13.wireOp",EDGE,"E61.MirrorCS")])],"isStart":true});
            var Q23;
            Q23=makeQuery(id+"F14.opExtrude","SWEPT_EDGE",EDGE,{"disambiguationData":[OSD([sQuery(id+"F13.wireOp",EDGE,"E64.MirrorCS"),sQuery(id+"F13.wireOp",EDGE,"E69.MirrorCS")])]});
            var Q24;
            Q24=makeQuery(id+"F14.opExtrude","CAP_EDGE",EDGE,{"disambiguationData":[OSD([sQuery(id+"F13.wireOp",EDGE,"E69.MirrorCS")])],"isStart":true});
            var Q25;
            Q25=makeQuery(id+"F14.opExtrude","SWEPT_EDGE",EDGE,{"disambiguationData":[OSD([sQuery(id+"F13.wireOp",EDGE,"E59.MirrorCS"),sQuery(id+"F13.wireOp",EDGE,"E69.MirrorCS")])]});
            var Q26;
            Q26=makeQuery(id+"F14.opExtrude","CAP_EDGE",EDGE,{"disambiguationData":[OSD([sQuery(id+"F13.wireOp",EDGE,"E69.MirrorCS")])],"isStart":false});
            fillet(context, id + "F17", {"entities" : qUnion([Q0, Q1, Q2, Q3, Q4, Q5, Q6, Q7, Q8, Q9, Q10, Q11, Q12, Q13, Q14, Q15, Q16, Q17, Q18, Q19, Q20, Q21, Q22, Q23, Q24, Q25, Q26]), "radius" : 0.25 * mm, "tangentPropagation" : true, "allowEdgeOverflow" : false});
        }
        {
            var Q0;
            Q0=makeQuery(id+"F14.opExtrude","SWEPT_FACE",FACE,{"disambiguationData":[OSD([sQuery(id+"F13.wireOp",EDGE,"E64.MirrorCS")])]});
            var sketch = newSketch(context, id + "F18", { "sketchPlane" : qUnion([Q0])});
            skPoint(sketch, "E73", {"position": v(-10.4, 0) * mm});
            skPoint(sketch, "E74", {"position": v(29.6, 0) * mm});
            skSolve(sketch);
        }
        {
            var Q0;
            Q0=sQuery(id+"F18.wireOp",VERTEX,"E73");
            var Q1;
            Q1=sQuery(id+"F18.wireOp",VERTEX,"E74");
            var Q2;
            Q2=makeQuery(id+"F14.opExtrude","SWEPT_BODY",BODY,{"disambiguationData":[OSD([sQuery(id+"F13.wireOp",EDGE,"E59.MirrorCS"),sQuery(id+"F13.wireOp",EDGE,"E60.MirrorCS"),sQuery(id+"F13.wireOp",EDGE,"E61.MirrorCS"),sQuery(id+"F13.wireOp",EDGE,"E63.MirrorCS"),sQuery(id+"F13.wireOp",EDGE,"E64.MirrorCS"),sQuery(id+"F13.wireOp",EDGE,"E65.MirrorCS"),sQuery(id+"F13.wireOp",EDGE,"E67.MirrorCS"),sQuery(id+"F13.wireOp",EDGE,"E68.MirrorCS"),sQuery(id+"F13.wireOp",EDGE,"E69.MirrorCS")])]});
            hole(context, id + "F19", {"style" : HoleStyle.C_BORE, "endStyle" : HoleEndStyle.BLIND, "holeDiameter" : 4 * mm, "cBoreDiameter" : 8 * mm, "cBoreDepth" : 2 * mm, "majorDiameter" : 5 * mm, "holeDepth" : 6.2 * mm, "isTappedThrough" : true, "tappedDepth" : 12 * mm, "tapClearance" : 3, "startFromSketch" : true, "locations" : qUnion([Q0, Q1]), "scope" : qUnion([Q2])});
        }
        {
            var Q0;
            Q0=makeQuery(id+"F7.boolean.opBoolean","COPY",FACE,{"derivedFrom":makeQuery(id+"F7.opExtrude","SWEPT_FACE",FACE,{"disambiguationData":[OSD([sQuery(id+"F6.wireOp",EDGE,"E29")])]})});
            var sketch = newSketch(context, id + "F20", { "sketchPlane" : qUnion([Q0])});
            skLineSegment(sketch, "E75.bottom", {"start": v(-6.08, -31.96) * mm, "end": v(-120.14, -31.96) * mm});
            skLineSegment(sketch, "E75.top", {"start": v(-6.08, 32.43) * mm, "end": v(-120.14, 32.43) * mm});
            skLineSegment(sketch, "E75.left", {"start": v(-6.08, -31.96) * mm, "end": v(-6.08, 32.43) * mm});
            skLineSegment(sketch, "E75.right", {"start": v(-120.14, -31.96) * mm, "end": v(-120.14, 32.43) * mm});
            skSolve(sketch);
        }
        {
            var Q0;
            Q0 = qSketchRegion(id + "F20", true);
            extrude(context, id + "F21", {"entities" : qUnion([Q0]), "operationType" : NewBodyOperationType.REMOVE, "depth" : 62 * mm, "offsetDistance" : 25 * mm});
        }
        {
            var Q0;
            {var subQ0=sQuery(id+"F0.wireOp",EDGE,"E8");var subQ1=sQuery(id+"F0.wireOp",EDGE,"E7");var subQ2=sQuery(id+"F0.wireOp",EDGE,"E6");var subQ3=sQuery(id+"F0.wireOp",EDGE,"E5");var subQ4=sQuery(id+"F0.wireOp",EDGE,"E4");var subQ5=sQuery(id+"F0.wireOp",EDGE,"E3");var subQ6=sQuery(id+"F0.wireOp",EDGE,"E2");var subQ7=sQuery(id+"F0.wireOp",EDGE,"E1");var subQ8=sQuery(id+"F0.wireOp",EDGE,"E0");var subQ9=sQuery(id+"F2.wireOp",EDGE,"E22");var subQ10=sQuery(id+"F2.wireOp",EDGE,"E23");Q0=makeQuery(id+"F21.boolean.opBoolean","INTERSECT",EDGE,{"derivedFrom":[makeQuery(id+"F3.boolean.opBoolean","SPLIT",FACE,{"disambiguationData":[TD([makeQuery(id+"F1.opExtrude","CAP_FACE",FACE,{"disambiguationData":[OSD([subQ8,subQ7,subQ6,subQ5,subQ4,subQ3,subQ2,subQ1,subQ0])],"isStart":true}),makeQuery(id+"F1.opExtrude","CAP_FACE",FACE,{"disambiguationData":[OSD([subQ8,subQ7,subQ6,subQ5,subQ4,subQ3,subQ2,subQ1,subQ0])],"isStart":false}),makeQuery(id+"F3.opExtrude","SWEPT_FACE",FACE,{"disambiguationData":[OSD([subQ9]),TDD([makeQuery(id+"F2.imprint","IMPRINT",EDGE,{"disambiguationData":[TD([[makeQuery(id+"F2.imprint","INTERSECT",VERTEX,{"disambiguationData":[OD(1.0)],"derivedFrom":[sQuery(id+"F2.wireOp",EDGE,"E21"),subQ9]}),1.0]])],"derivedFrom":subQ9})])]}),makeQuery(id+"F3.opExtrude","SWEPT_FACE",FACE,{"disambiguationData":[OSD([subQ10])]})])],"derivedFrom":makeQuery(id+"F1.opExtrude","SWEPT_FACE",FACE,{"disambiguationData":[OSD([subQ6])]})}),makeQuery(id+"F21.opExtrude","CAP_FACE",FACE,{"disambiguationData":[OSD([sQuery(id+"F20.wireOp",EDGE,"E75.bottom"),sQuery(id+"F20.wireOp",EDGE,"E75.top"),sQuery(id+"F20.wireOp",EDGE,"E75.left"),sQuery(id+"F20.wireOp",EDGE,"E75.right")])],"isStart":true})]});}
            fillet(context, id + "F22", {"entities" : qUnion([Q0]), "radius" : 5 * mm, "tangentPropagation" : true, "allowEdgeOverflow" : false});
        }
    });
